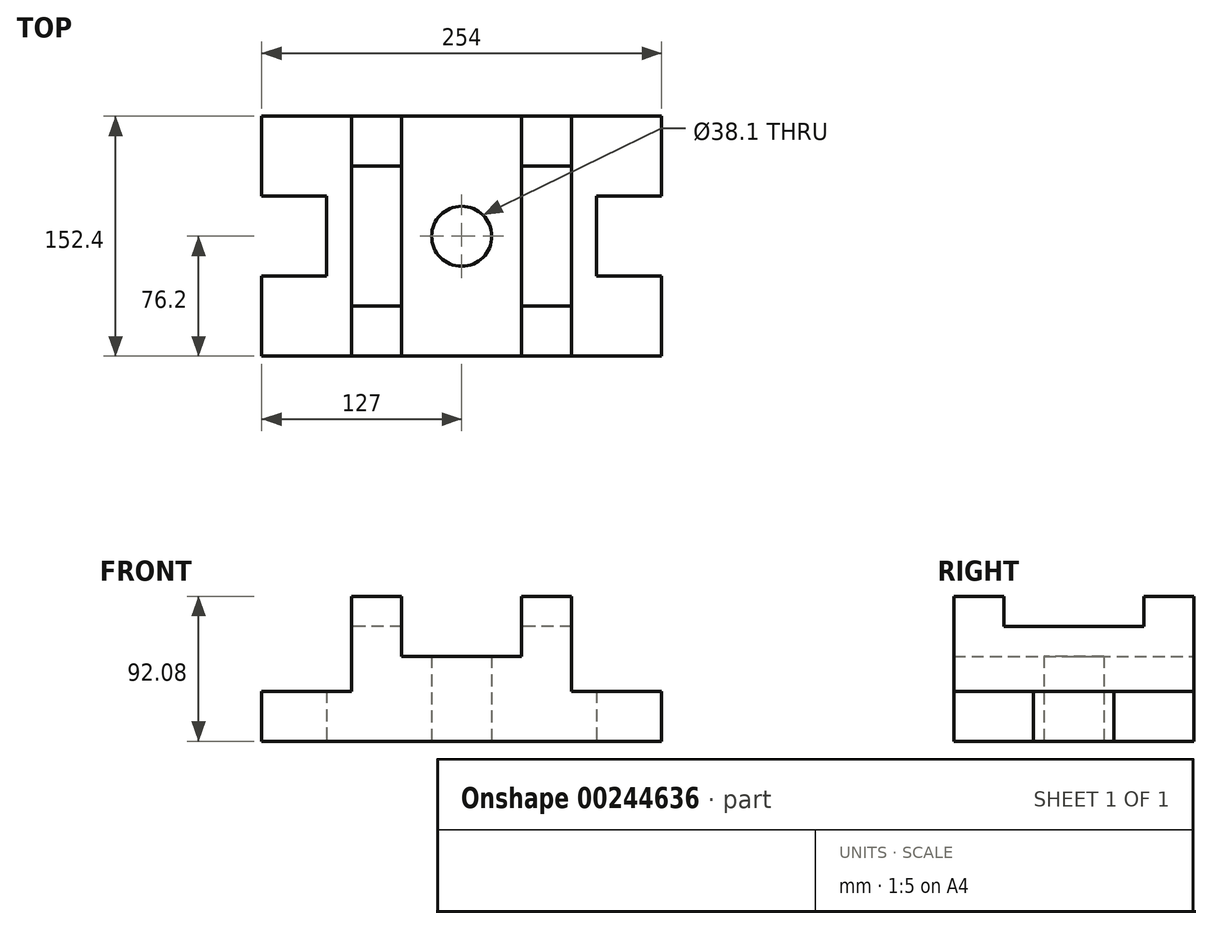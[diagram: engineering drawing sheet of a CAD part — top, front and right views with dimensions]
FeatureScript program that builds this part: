
annotation { "Feature Type Name" : "Feature", "Feature Type Description" : "" }
export const myFeature = defineFeature(function(context is Context, id is Id, definition is map)
    precondition{}
    {
        {
            var Q0;
            Q0=qCreatedBy(makeId("Top.planeOp"),FACE);
            var sketch = newSketch(context, id + "F0", { "sketchPlane" : qUnion([Q0])});
            skLineSegment(sketch, "E0.bottom", {"start": v(-127, 76.2) * mm, "end": v(127, 76.2) * mm});
            skLineSegment(sketch, "E0.top", {"start": v(-127, -76.2) * mm, "end": v(127, -76.2) * mm});
            skLineSegment(sketch, "E0.left", {"start": v(-127, 76.2) * mm, "end": v(-127, 25.4) * mm});
            skLineSegment(sketch, "E0.right", {"start": v(127, 76.2) * mm, "end": v(127, 25.4) * mm});
            skLineSegment(sketch, "E1", {"start": v(-69.85, 76.2) * mm, "end": v(-69.85, -76.2) * mm});
            skLineSegment(sketch, "E2", {"start": v(-38.1, 76.2) * mm, "end": v(-38.1, -76.2) * mm});
            skLineSegment(sketch, "E3", {"start": v(38.1, 76.2) * mm, "end": v(38.1, -76.2) * mm});
            skLineSegment(sketch, "E4", {"start": v(69.85, 76.2) * mm, "end": v(69.85, -76.2) * mm});
            skLineSegment(sketch, "E5", {"start": v(-69.85, 44.45) * mm, "end": v(-38.1, 44.45) * mm});
            skLineSegment(sketch, "E6", {"start": v(-69.85, -44.45) * mm, "end": v(-38.1, -44.45) * mm});
            skLineSegment(sketch, "E7", {"start": v(38.1, 44.45) * mm, "end": v(69.85, 44.45) * mm});
            skLineSegment(sketch, "E8", {"start": v(38.1, -44.45) * mm, "end": v(69.85, -44.45) * mm});
            skLineSegment(sketch, "E9.bottom", {"start": v(-127, 25.4) * mm, "end": v(-85.73, 25.4) * mm});
            skLineSegment(sketch, "E9.top", {"start": v(-127, -25.4) * mm, "end": v(-85.73, -25.4) * mm});
            skLineSegment(sketch, "E9.right", {"start": v(-85.73, 25.4) * mm, "end": v(-85.73, -25.4) * mm});
            skLineSegment(sketch, "E10.bottom", {"start": v(127, 25.4) * mm, "end": v(85.72, 25.4) * mm});
            skLineSegment(sketch, "E10.top", {"start": v(127, -25.4) * mm, "end": v(85.72, -25.4) * mm});
            skLineSegment(sketch, "E10.right", {"start": v(85.73, 25.4) * mm, "end": v(85.73, -25.4) * mm});
            skLineSegment(sketch, "E11.trimOffspring", {"start": v(-127, -25.4) * mm, "end": v(-127, -76.2) * mm});
            skLineSegment(sketch, "E12.trimOffspring", {"start": v(127, -25.4) * mm, "end": v(127, -76.2) * mm});
            skPoint(sketch, "E13.centerSnap0", {"position": v(-38.1, 0) * mm});
            skCircle(sketch, "E14", {"center": v(0, 0) * mm, "radius": 19.05 * mm});
            skSolve(sketch);
        }
        {
            var Q0;
            {var subQ7=sQuery(id+"F0.wireOp",EDGE,"E0.left");Q0=makeQuery(id+"F0.imprint","IMPRINT",FACE,{"disambiguationData":[TD([[makeQuery(id+"F0.imprint","IMPRINT",EDGE,{"derivedFrom":subQ7}),1.0]])]});}
            var Q1;
            {var subQ0=sQuery(id+"F0.wireOp",EDGE,"E0.right");Q1=makeQuery(id+"F0.imprint","IMPRINT",FACE,{"disambiguationData":[TD([[makeQuery(id+"F0.imprint","IMPRINT",EDGE,{"derivedFrom":subQ0}),-1.0]])]});}
            var Q2;
            {var subQ5=sQuery(id+"F0.wireOp",EDGE,"E5");Q2=makeQuery(id+"F0.imprint","IMPRINT",FACE,{"disambiguationData":[TD([[makeQuery(id+"F0.imprint","IMPRINT",EDGE,{"derivedFrom":subQ5}),1.0]])]});}
            var Q3;
            {var subQ0=sQuery(id+"F0.wireOp",EDGE,"E5");Q3=makeQuery(id+"F0.imprint","IMPRINT",FACE,{"disambiguationData":[TD([[makeQuery(id+"F0.imprint","IMPRINT",EDGE,{"derivedFrom":subQ0}),-1.0]])]});}
            var Q4;
            Q4=makeQuery(id+"F0.imprint","IMPRINT",FACE,{"disambiguationData":[TD([[makeQuery(id+"F0.imprint","IMPRINT",EDGE,{"derivedFrom":sQuery(id+"F0.wireOp",EDGE,"E14")}),-1.0]])]});
            var Q5;
            {var subQ5=sQuery(id+"F0.wireOp",EDGE,"E6");Q5=makeQuery(id+"F0.imprint","IMPRINT",FACE,{"disambiguationData":[TD([[makeQuery(id+"F0.imprint","IMPRINT",EDGE,{"derivedFrom":subQ5}),-1.0]])]});}
            var Q6;
            {var subQ5=sQuery(id+"F0.wireOp",EDGE,"E7");Q6=makeQuery(id+"F0.imprint","IMPRINT",FACE,{"disambiguationData":[TD([[makeQuery(id+"F0.imprint","IMPRINT",EDGE,{"derivedFrom":subQ5}),1.0]])]});}
            var Q7;
            {var subQ0=sQuery(id+"F0.wireOp",EDGE,"E7");Q7=makeQuery(id+"F0.imprint","IMPRINT",FACE,{"disambiguationData":[TD([[makeQuery(id+"F0.imprint","IMPRINT",EDGE,{"derivedFrom":subQ0}),-1.0]])]});}
            var Q8;
            {var subQ5=sQuery(id+"F0.wireOp",EDGE,"E8");Q8=makeQuery(id+"F0.imprint","IMPRINT",FACE,{"disambiguationData":[TD([[makeQuery(id+"F0.imprint","IMPRINT",EDGE,{"derivedFrom":subQ5}),-1.0]])]});}
            extrude(context, id + "F1", {"entities" : qUnion([Q0, Q1, Q2, Q3, Q4, Q5, Q6, Q7, Q8]), "depth" : 31.75 * mm});
        }
        {
            var Q0;
            {var subQ5=sQuery(id+"F0.wireOp",EDGE,"E7");Q0=makeQuery(id+"F0.imprint","IMPRINT",FACE,{"disambiguationData":[TD([[makeQuery(id+"F0.imprint","IMPRINT",EDGE,{"derivedFrom":subQ5}),1.0]])]});}
            var Q1;
            {var subQ0=sQuery(id+"F0.wireOp",EDGE,"E7");Q1=makeQuery(id+"F0.imprint","IMPRINT",FACE,{"disambiguationData":[TD([[makeQuery(id+"F0.imprint","IMPRINT",EDGE,{"derivedFrom":subQ0}),-1.0]])]});}
            var Q2;
            {var subQ5=sQuery(id+"F0.wireOp",EDGE,"E8");Q2=makeQuery(id+"F0.imprint","IMPRINT",FACE,{"disambiguationData":[TD([[makeQuery(id+"F0.imprint","IMPRINT",EDGE,{"derivedFrom":subQ5}),-1.0]])]});}
            var Q3;
            Q3=makeQuery(id+"F0.imprint","IMPRINT",FACE,{"disambiguationData":[TD([[makeQuery(id+"F0.imprint","IMPRINT",EDGE,{"derivedFrom":sQuery(id+"F0.wireOp",EDGE,"E14")}),-1.0]])]});
            var Q4;
            {var subQ5=sQuery(id+"F0.wireOp",EDGE,"E6");Q4=makeQuery(id+"F0.imprint","IMPRINT",FACE,{"disambiguationData":[TD([[makeQuery(id+"F0.imprint","IMPRINT",EDGE,{"derivedFrom":subQ5}),-1.0]])]});}
            var Q5;
            {var subQ0=sQuery(id+"F0.wireOp",EDGE,"E5");Q5=makeQuery(id+"F0.imprint","IMPRINT",FACE,{"disambiguationData":[TD([[makeQuery(id+"F0.imprint","IMPRINT",EDGE,{"derivedFrom":subQ0}),-1.0]])]});}
            var Q6;
            {var subQ5=sQuery(id+"F0.wireOp",EDGE,"E5");Q6=makeQuery(id+"F0.imprint","IMPRINT",FACE,{"disambiguationData":[TD([[makeQuery(id+"F0.imprint","IMPRINT",EDGE,{"derivedFrom":subQ5}),1.0]])]});}
            extrude(context, id + "F2", {"entities" : qUnion([Q0, Q1, Q2, Q3, Q4, Q5, Q6]), "operationType" : NewBodyOperationType.ADD, "depth" : 53.97 * mm});
        }
        {
            var Q0;
            {var subQ0=sQuery(id+"F0.wireOp",EDGE,"E5");Q0=makeQuery(id+"F0.imprint","IMPRINT",FACE,{"disambiguationData":[TD([[makeQuery(id+"F0.imprint","IMPRINT",EDGE,{"derivedFrom":subQ0}),-1.0]])]});}
            var Q1;
            {var subQ0=sQuery(id+"F0.wireOp",EDGE,"E7");Q1=makeQuery(id+"F0.imprint","IMPRINT",FACE,{"disambiguationData":[TD([[makeQuery(id+"F0.imprint","IMPRINT",EDGE,{"derivedFrom":subQ0}),-1.0]])]});}
            var Q2;
            {var subQ5=sQuery(id+"F0.wireOp",EDGE,"E5");Q2=makeQuery(id+"F0.imprint","IMPRINT",FACE,{"disambiguationData":[TD([[makeQuery(id+"F0.imprint","IMPRINT",EDGE,{"derivedFrom":subQ5}),1.0]])]});}
            var Q3;
            {var subQ5=sQuery(id+"F0.wireOp",EDGE,"E6");Q3=makeQuery(id+"F0.imprint","IMPRINT",FACE,{"disambiguationData":[TD([[makeQuery(id+"F0.imprint","IMPRINT",EDGE,{"derivedFrom":subQ5}),-1.0]])]});}
            var Q4;
            {var subQ5=sQuery(id+"F0.wireOp",EDGE,"E7");Q4=makeQuery(id+"F0.imprint","IMPRINT",FACE,{"disambiguationData":[TD([[makeQuery(id+"F0.imprint","IMPRINT",EDGE,{"derivedFrom":subQ5}),1.0]])]});}
            var Q5;
            {var subQ5=sQuery(id+"F0.wireOp",EDGE,"E8");Q5=makeQuery(id+"F0.imprint","IMPRINT",FACE,{"disambiguationData":[TD([[makeQuery(id+"F0.imprint","IMPRINT",EDGE,{"derivedFrom":subQ5}),-1.0]])]});}
            extrude(context, id + "F3", {"entities" : qUnion([Q0, Q1, Q2, Q3, Q4, Q5]), "operationType" : NewBodyOperationType.ADD, "depth" : 73.02 * mm});
        }
        {
            var Q0;
            {var subQ5=sQuery(id+"F0.wireOp",EDGE,"E5");Q0=makeQuery(id+"F0.imprint","IMPRINT",FACE,{"disambiguationData":[TD([[makeQuery(id+"F0.imprint","IMPRINT",EDGE,{"derivedFrom":subQ5}),1.0]])]});}
            var Q1;
            {var subQ5=sQuery(id+"F0.wireOp",EDGE,"E6");Q1=makeQuery(id+"F0.imprint","IMPRINT",FACE,{"disambiguationData":[TD([[makeQuery(id+"F0.imprint","IMPRINT",EDGE,{"derivedFrom":subQ5}),-1.0]])]});}
            var Q2;
            {var subQ5=sQuery(id+"F0.wireOp",EDGE,"E7");Q2=makeQuery(id+"F0.imprint","IMPRINT",FACE,{"disambiguationData":[TD([[makeQuery(id+"F0.imprint","IMPRINT",EDGE,{"derivedFrom":subQ5}),1.0]])]});}
            var Q3;
            {var subQ5=sQuery(id+"F0.wireOp",EDGE,"E8");Q3=makeQuery(id+"F0.imprint","IMPRINT",FACE,{"disambiguationData":[TD([[makeQuery(id+"F0.imprint","IMPRINT",EDGE,{"derivedFrom":subQ5}),-1.0]])]});}
            extrude(context, id + "F4", {"entities" : qUnion([Q0, Q1, Q2, Q3]), "operationType" : NewBodyOperationType.ADD, "depth" : 92.07 * mm});
        }
    });
